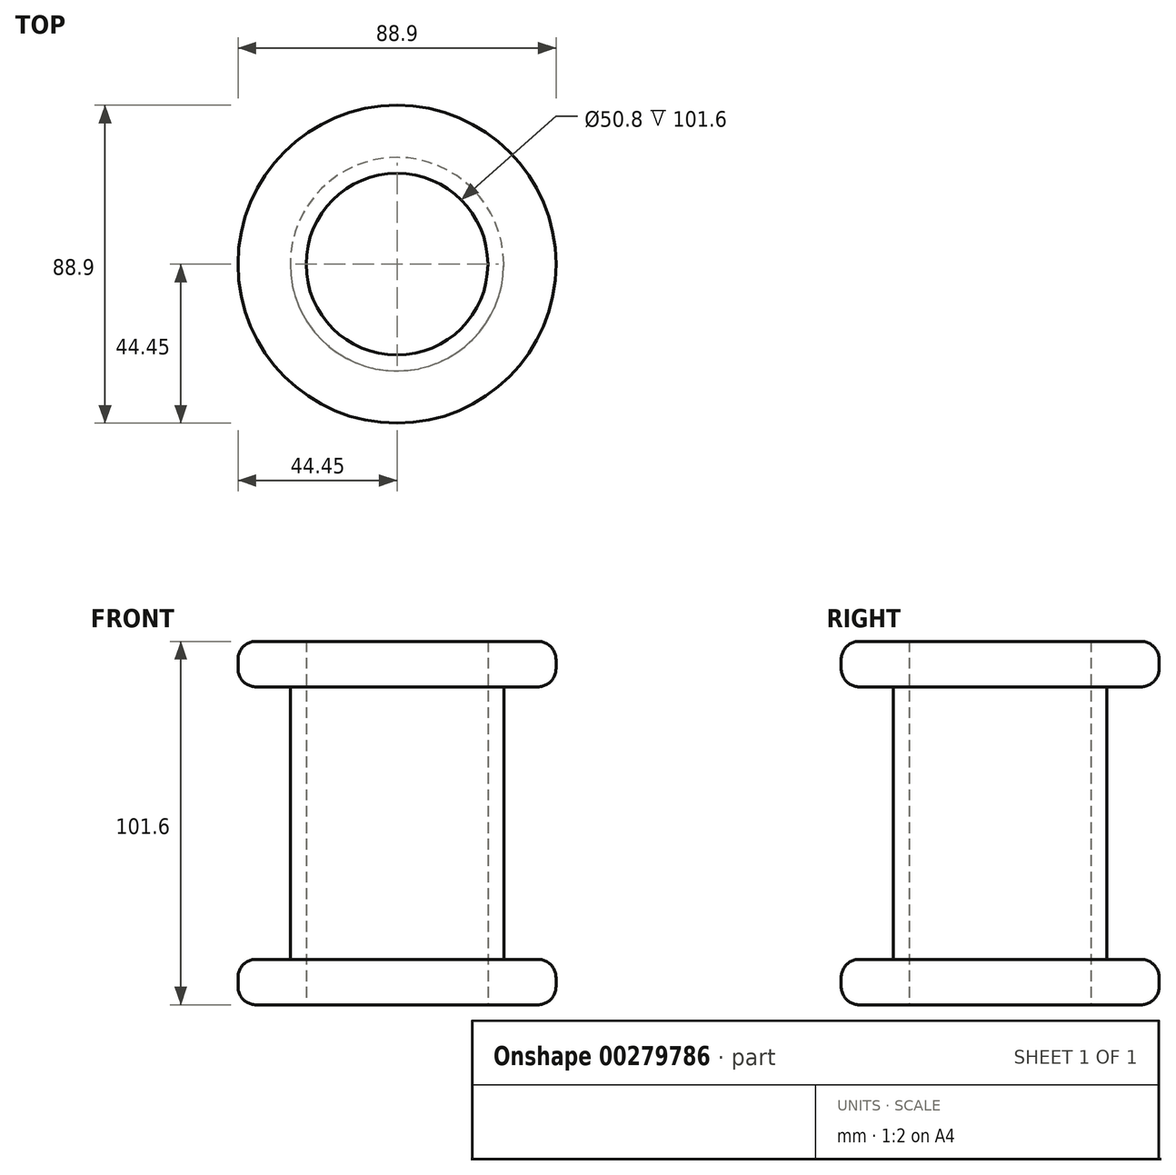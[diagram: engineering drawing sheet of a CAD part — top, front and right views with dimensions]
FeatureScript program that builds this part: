
annotation { "Feature Type Name" : "Feature", "Feature Type Description" : "" }
export const myFeature = defineFeature(function(context is Context, id is Id, definition is map)
    precondition{}
    {
        {
            var Q0;
            Q0=qCreatedBy(makeId("Top.planeOp"),FACE);
            var sketch = newSketch(context, id + "F0", { "sketchPlane" : qUnion([Q0])});
            skCircle(sketch, "E0", {"center": v(0, 0) * mm, "radius": 25.4 * mm});
            skCircle(sketch, "E1", {"center": v(0, 0) * mm, "radius": 29.85 * mm});
            skSolve(sketch);
        }
        {
            var Q0;
            Q0 = qSketchRegion(id + "F0", true);
            extrude(context, id + "F1", {"entities" : qUnion([Q0]), "endBound" : BoundingType.SYMMETRIC, "depth" : 101.6 * mm});
        }
        {
            var Q0;
            Q0=makeQuery(id+"F1.opExtrude","CAP_FACE",FACE,{"disambiguationData":[OSD([sQuery(id+"F0.wireOp",EDGE,"E0"),sQuery(id+"F0.wireOp",EDGE,"E1")])],"isStart":true});
            var sketch = newSketch(context, id + "F2", { "sketchPlane" : qUnion([Q0])});
            skCircle(sketch, "E2", {"center": v(0, 0) * mm, "radius": 44.45 * mm});
            skSolve(sketch);
        }
        {
            var Q0;
            Q0 = qSketchRegion(id + "F2", true);
            extrude(context, id + "F3", {"entities" : qUnion([Q0]), "operationType" : NewBodyOperationType.ADD, "oppositeDirection" : true, "depth" : 12.7 * mm});
        }
        {
            var Q0;
            Q0=makeQuery(id+"F3.opExtrude","SWEPT_FACE",FACE,{"disambiguationData":[OSD([sQuery(id+"F2.wireOp",EDGE,"E2")])]});
            fillet(context, id + "F4", {"entities" : qUnion([Q0]), "radius" : 5.08 * mm, "tangentPropagation" : true, "allowEdgeOverflow" : false});
        }
        {
            var Q0;
            Q0=makeQuery(id+"F3.boolean.opBoolean","MERGE",FACE,{"derivedFrom":[makeQuery(id+"F1.opExtrude","CAP_FACE",FACE,{"disambiguationData":[OSD([sQuery(id+"F0.wireOp",EDGE,"E0"),sQuery(id+"F0.wireOp",EDGE,"E1")])],"isStart":true}),makeQuery(id+"F3.opExtrude","CAP_FACE",FACE,{"disambiguationData":[OSD([sQuery(id+"F2.wireOp",EDGE,"E2")])],"isStart":true})]});
            var sketch = newSketch(context, id + "F5", { "sketchPlane" : qUnion([Q0])});
            skCircle(sketch, "E3", {"center": v(0, 0) * mm, "radius": 25.4 * mm});
            skSolve(sketch);
        }
        {
            var Q0;
            Q0=sQuery(id+"F5.wireOp",VERTEX,"E3.center");
            var Q1;
            Q1=makeQuery(id+"F1.opExtrude","SWEPT_BODY",BODY,{"disambiguationData":[OSD([sQuery(id+"F0.wireOp",EDGE,"E0"),sQuery(id+"F0.wireOp",EDGE,"E1")])]});
            hole(context, id + "F6", {"style" : HoleStyle.SIMPLE, "endStyle" : HoleEndStyle.THROUGH, "holeDiameter" : 50.8 * mm, "tappedDepth" : 12.7 * mm, "tapClearance" : 3, "locations" : qUnion([Q0]), "scope" : qUnion([Q1])});
        }
        {
            var Q0;
            Q0=makeQuery(id+"F1.opExtrude","CAP_FACE",FACE,{"disambiguationData":[OSD([sQuery(id+"F0.wireOp",EDGE,"E0"),sQuery(id+"F0.wireOp",EDGE,"E1")])],"isStart":false});
            var sketch = newSketch(context, id + "F7", { "sketchPlane" : qUnion([Q0])});
            skCircle(sketch, "E4", {"center": v(0, 0) * mm, "radius": 44.45 * mm});
            skSolve(sketch);
        }
        {
            var Q0;
            Q0 = qSketchRegion(id + "F7", true);
            extrude(context, id + "F8", {"entities" : qUnion([Q0]), "operationType" : NewBodyOperationType.ADD, "oppositeDirection" : true, "depth" : 12.7 * mm});
        }
        {
            var Q0;
            Q0=makeQuery(id+"F8.opExtrude","SWEPT_FACE",FACE,{"disambiguationData":[OSD([sQuery(id+"F7.wireOp",EDGE,"E4")])]});
            fillet(context, id + "F9", {"entities" : qUnion([Q0]), "radius" : 5.08 * mm, "tangentPropagation" : true, "allowEdgeOverflow" : false});
        }
        {
            var Q0;
            Q0=makeQuery(id+"F8.boolean.opBoolean","MERGE",FACE,{"derivedFrom":[makeQuery(id+"F1.opExtrude","CAP_FACE",FACE,{"disambiguationData":[OSD([sQuery(id+"F0.wireOp",EDGE,"E0"),sQuery(id+"F0.wireOp",EDGE,"E1")])],"isStart":false}),makeQuery(id+"F8.opExtrude","CAP_FACE",FACE,{"disambiguationData":[OSD([sQuery(id+"F7.wireOp",EDGE,"E4")])],"isStart":true})]});
            var sketch = newSketch(context, id + "F10", { "sketchPlane" : qUnion([Q0])});
            skCircle(sketch, "E5", {"center": v(0, 0) * mm, "radius": 25.4 * mm});
            skSolve(sketch);
        }
        {
            var Q0;
            Q0=sQuery(id+"F10.wireOp",VERTEX,"E5.center");
            var Q1;
            Q1=makeQuery(id+"F1.opExtrude","SWEPT_BODY",BODY,{"disambiguationData":[OSD([sQuery(id+"F0.wireOp",EDGE,"E0"),sQuery(id+"F0.wireOp",EDGE,"E1")])]});
            hole(context, id + "F11", {"style" : HoleStyle.SIMPLE, "endStyle" : HoleEndStyle.THROUGH, "holeDiameter" : 50.8 * mm, "tappedDepth" : 12.7 * mm, "tapClearance" : 3, "locations" : qUnion([Q0]), "scope" : qUnion([Q1])});
        }
    });
